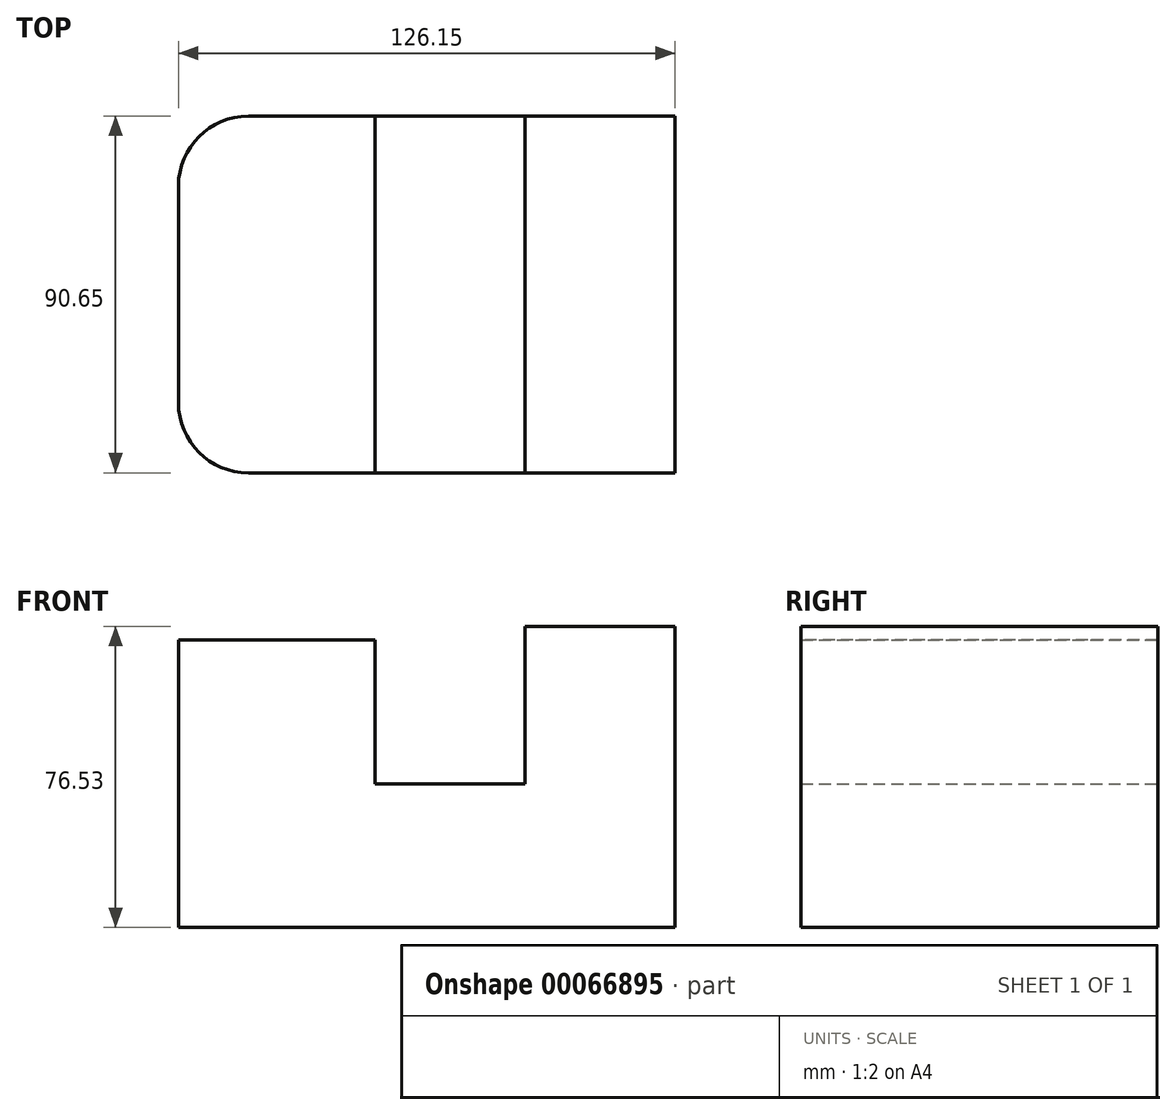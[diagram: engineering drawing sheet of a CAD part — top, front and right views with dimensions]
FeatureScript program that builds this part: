
annotation { "Feature Type Name" : "Feature", "Feature Type Description" : "" }
export const myFeature = defineFeature(function(context is Context, id is Id, definition is map)
    precondition{}
    {
        {
            var Q0;
            Q0=qCreatedBy(makeId("Top.planeOp"),FACE);
            var sketch = newSketch(context, id + "F0", { "sketchPlane" : qUnion([Q0])});
            skLineSegment(sketch, "E0.bottom", {"start": v(-100.65, 31.12) * mm, "end": v(-29.34, 31.12) * mm});
            skLineSegment(sketch, "E0.top", {"start": v(-100.65, -59.53) * mm, "end": v(-29.34, -59.53) * mm});
            skLineSegment(sketch, "E0.left", {"start": v(-118.43, 13.34) * mm, "end": v(-118.43, -41.75) * mm});
            skLineSegment(sketch, "E0.right", {"start": v(-11.56, 13.34) * mm, "end": v(-11.56, -41.75) * mm});
            skPoint(sketch, "E1.visualSharp", {"position": v(-118.43, 31.12) * mm});
            skArc(sketch, "E1.filletArc", {"start": v(-100.65, 31.12) * mm, "mid": v(-113.22, 25.9) * mm, "end": v(-118.43, 13.34) * mm});
            skPoint(sketch, "E2.visualSharp", {"position": v(-11.56, 31.12) * mm});
            skArc(sketch, "E2.filletArc", {"start": v(-11.56, 13.34) * mm, "mid": v(-16.77, 25.9) * mm, "end": v(-29.34, 31.12) * mm});
            skPoint(sketch, "E3.visualSharp", {"position": v(-11.56, -59.53) * mm});
            skArc(sketch, "E3.filletArc", {"start": v(-29.34, -59.53) * mm, "mid": v(-16.77, -54.32) * mm, "end": v(-11.56, -41.75) * mm});
            skPoint(sketch, "E4.visualSharp", {"position": v(-118.43, -59.53) * mm});
            skArc(sketch, "E4.filletArc", {"start": v(-118.43, -41.75) * mm, "mid": v(-113.22, -54.32) * mm, "end": v(-100.65, -59.53) * mm});
            skLineSegment(sketch, "E5", {"start": v(-68.48, -59.53) * mm, "end": v(-68.48, 31.12) * mm});
            skSolve(sketch);
        }
        {
            var Q0;
            Q0=makeQuery(id+"F0.imprint","IMPRINT",FACE,{"disambiguationData":[TD([[makeQuery(id+"F0.imprint","IMPRINT",EDGE,{"derivedFrom":sQuery(id+"F0.wireOp",EDGE,"E0.left")}),1.0]])]});
            extrude(context, id + "F1", {"entities" : qUnion([Q0]), "depth" : 73.06 * mm});
        }
        {
            var Q0;
            Q0=makeQuery(id+"F1.opExtrude","SWEPT_FACE",FACE,{"disambiguationData":[OSD([sQuery(id+"F0.wireOp",EDGE,"E5")])]});
            var sketch = newSketch(context, id + "F2", { "sketchPlane" : qUnion([Q0])});
            skLineSegment(sketch, "E6", {"start": v(-59.53, 36.53) * mm, "end": v(31.12, 36.53) * mm});
            skSolve(sketch);
        }
        {
            var Q0;
            {var subQ0=sQuery(id+"F2.wireOp",EDGE,"E6");Q0=makeQuery(id+"F2.imprint","IMPRINT",FACE,{"disambiguationData":[TD([[makeQuery(id+"F2.imprint","IMPRINT",EDGE,{"derivedFrom":subQ0}),-1.0]])]});}
            extrude(context, id + "F3", {"entities" : qUnion([Q0]), "operationType" : NewBodyOperationType.ADD, "depth" : 76.2 * mm});
        }
        {
            var Q0;
            Q0=makeQuery(id+"F3.opExtrude","SWEPT_FACE",FACE,{"disambiguationData":[OSD([sQuery(id+"F2.wireOp",EDGE,"E6")])]});
            var sketch = newSketch(context, id + "F4", { "sketchPlane" : qUnion([Q0])});
            skLineSegment(sketch, "E7", {"start": v(-30.38, 31.12) * mm, "end": v(-30.38, -59.53) * mm});
            skSolve(sketch);
        }
        {
            var Q0;
            {var subQ0=sQuery(id+"F4.wireOp",EDGE,"E7");Q0=makeQuery(id+"F4.imprint","IMPRINT",FACE,{"disambiguationData":[TD([[makeQuery(id+"F4.imprint","IMPRINT",EDGE,{"derivedFrom":subQ0}),1.0]])]});}
            extrude(context, id + "F5", {"entities" : qUnion([Q0]), "operationType" : NewBodyOperationType.ADD, "depth" : 40 * mm});
        }
    });
